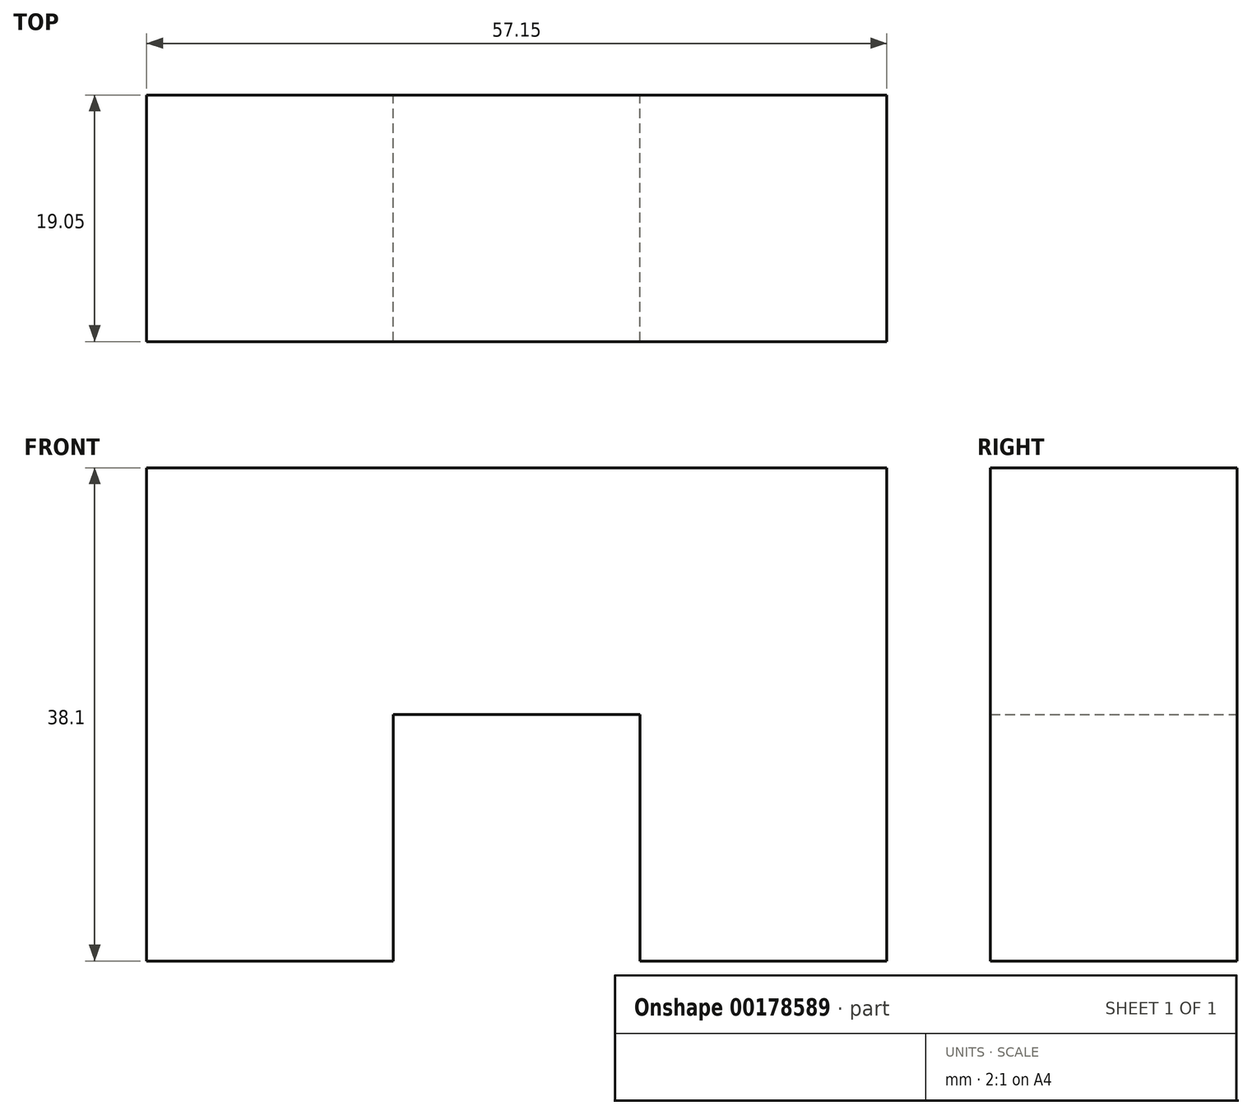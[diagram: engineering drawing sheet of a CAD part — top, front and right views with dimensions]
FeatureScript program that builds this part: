
annotation { "Feature Type Name" : "Feature", "Feature Type Description" : "" }
export const myFeature = defineFeature(function(context is Context, id is Id, definition is map)
    precondition{}
    {
        {
            var Q0;
            Q0=qCreatedBy(makeId("Front.planeOp"),FACE);
            var sketch = newSketch(context, id + "F0", { "sketchPlane" : qUnion([Q0])});
            skLineSegment(sketch, "E0", {"start": v(-38.1, 38.1) * mm, "end": v(-19.05, 38.1) * mm});
            skLineSegment(sketch, "E1", {"start": v(-19.05, 38.1) * mm, "end": v(-19.05, 19.05) * mm});
            skLineSegment(sketch, "E2", {"start": v(-19.05, 19.05) * mm, "end": v(-38.1, 19.05) * mm});
            skLineSegment(sketch, "E3", {"start": v(-38.1, 19.05) * mm, "end": v(-38.1, 38.1) * mm});
            skLineSegment(sketch, "E4", {"start": v(-38.1, 19.05) * mm, "end": v(-38.1, 0) * mm});
            skLineSegment(sketch, "E5", {"start": v(-19.05, 19.05) * mm, "end": v(-19.05, 0) * mm});
            skLineSegment(sketch, "E6", {"start": v(-19.05, 0) * mm, "end": v(-38.1, 0) * mm});
            skLineSegment(sketch, "E7", {"start": v(-19.05, 38.1) * mm, "end": v(0, 38.1) * mm});
            skLineSegment(sketch, "E8", {"start": v(0, 38.1) * mm, "end": v(0, 19.05) * mm});
            skLineSegment(sketch, "E9", {"start": v(0, 19.05) * mm, "end": v(-19.05, 19.05) * mm});
            skLineSegment(sketch, "E10", {"start": v(0, 38.1) * mm, "end": v(19.05, 38.1) * mm});
            skLineSegment(sketch, "E11", {"start": v(19.05, 38.1) * mm, "end": v(19.05, 19.05) * mm});
            skLineSegment(sketch, "E12", {"start": v(19.05, 19.05) * mm, "end": v(0, 19.05) * mm});
            skLineSegment(sketch, "E13", {"start": v(0, 19.05) * mm, "end": v(0, 0) * mm});
            skLineSegment(sketch, "E14", {"start": v(0, 0) * mm, "end": v(19.05, 0) * mm});
            skLineSegment(sketch, "E15", {"start": v(19.05, 0) * mm, "end": v(19.05, 19.05) * mm});
            skSolve(sketch);
        }
        {
            var Q0;
            Q0 = qSketchRegion(id + "F0", true);
            extrude(context, id + "F1", {"entities" : qUnion([Q0]), "depth" : 19.05 * mm});
        }
    });
